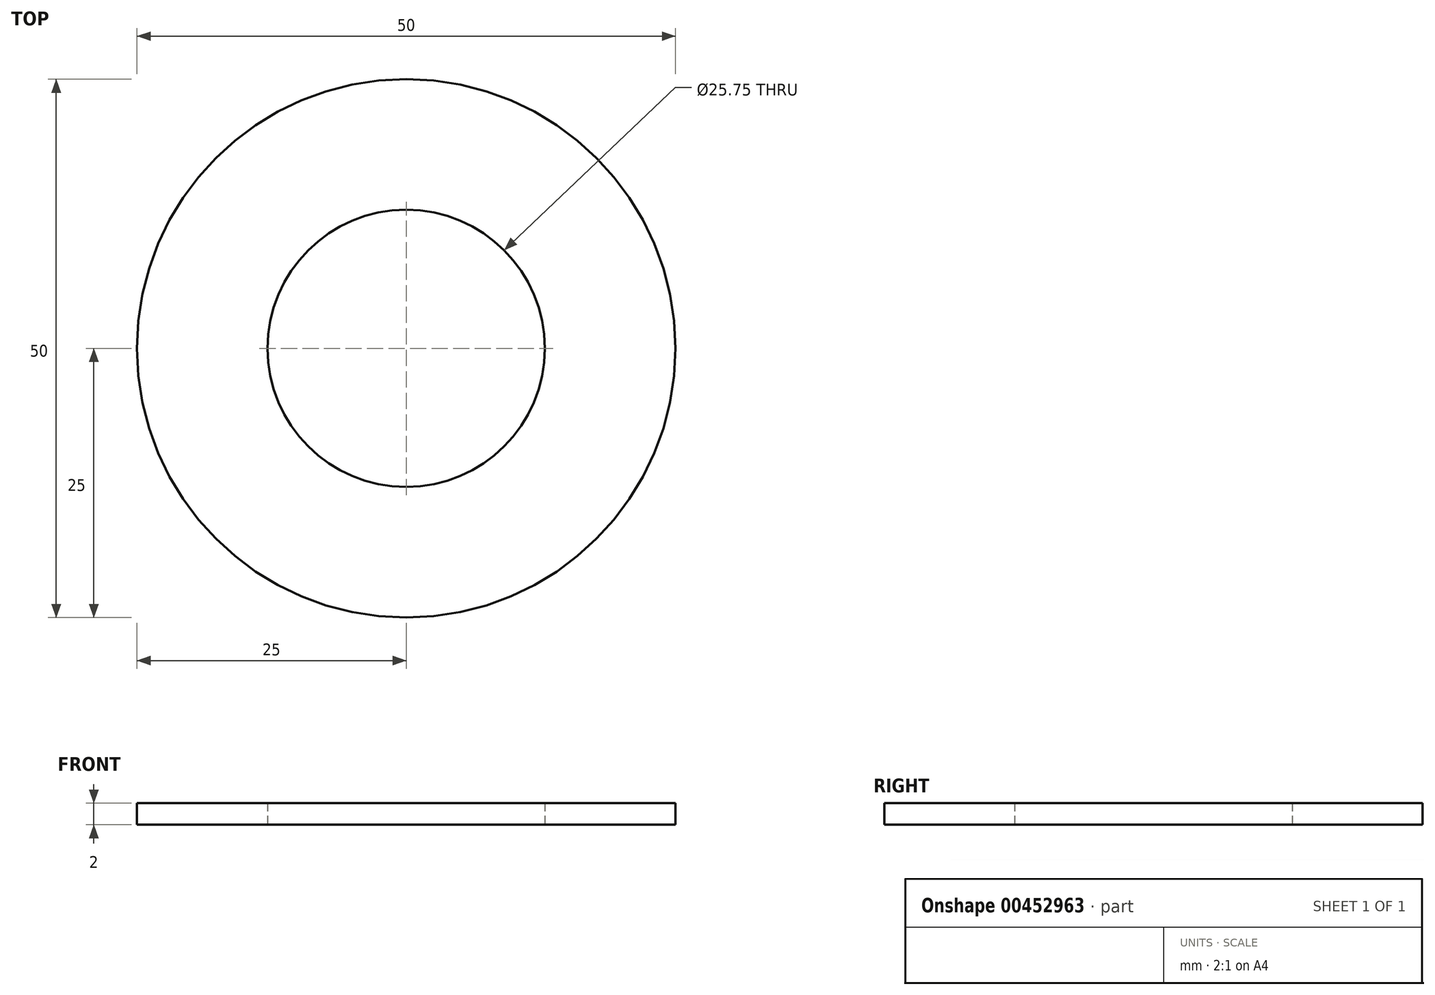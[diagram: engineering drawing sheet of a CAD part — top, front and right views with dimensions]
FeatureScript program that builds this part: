
annotation { "Feature Type Name" : "Feature", "Feature Type Description" : "" }
export const myFeature = defineFeature(function(context is Context, id is Id, definition is map)
    precondition{}
    {
        {
            var Q0;
            Q0=qCreatedBy(makeId("Top.planeOp"),FACE);
            var sketch = newSketch(context, id + "F0", { "sketchPlane" : qUnion([Q0])});
            skCircle(sketch, "E0", {"center": v(0, 0) * mm, "radius": 25 * mm});
            skCircle(sketch, "E1", {"center": v(0, 0) * mm, "radius": 12.88 * mm});
            skSolve(sketch);
        }
        {
            var Q0;
            Q0 = qSketchRegion(id + "F0", true);
            extrude(context, id + "F1", {"entities" : qUnion([Q0]), "depth" : 2 * mm});
        }
    });
